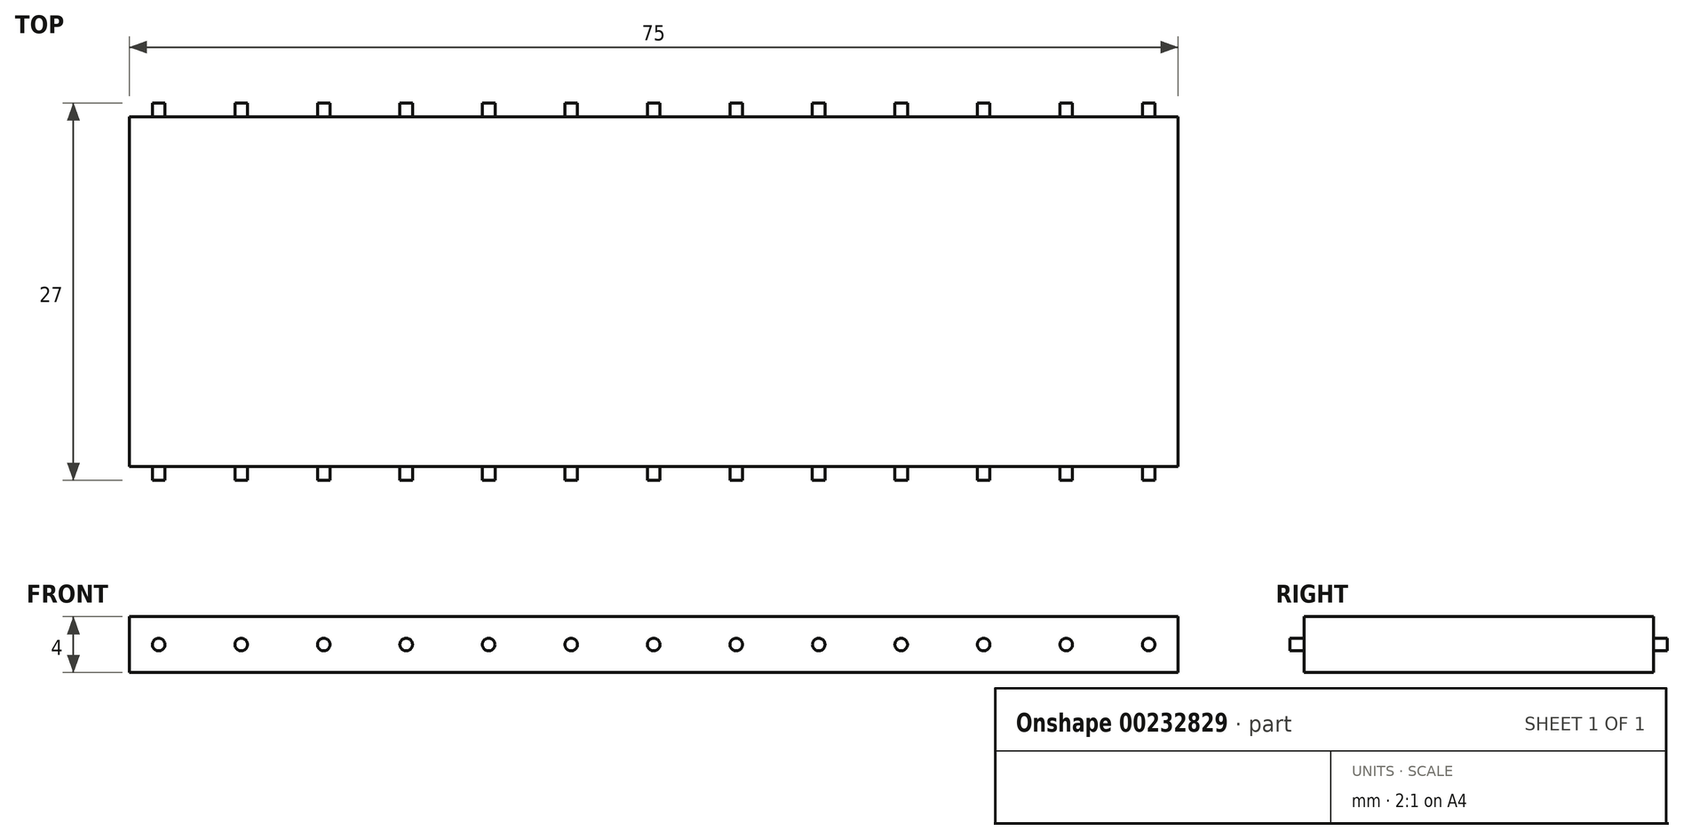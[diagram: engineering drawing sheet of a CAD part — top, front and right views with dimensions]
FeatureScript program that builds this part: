
annotation { "Feature Type Name" : "Feature", "Feature Type Description" : "" }
export const myFeature = defineFeature(function(context is Context, id is Id, definition is map)
    precondition{}
    {
        {
            var Q0;
            Q0=qCreatedBy(makeId("Top.planeOp"),FACE);
            var sketch = newSketch(context, id + "F0", { "sketchPlane" : qUnion([Q0])});
            skLineSegment(sketch, "E0.bottom", {"start": v(37.5, -12.5) * mm, "end": v(-37.5, -12.5) * mm});
            skLineSegment(sketch, "E0.top", {"start": v(37.5, 12.5) * mm, "end": v(-37.5, 12.5) * mm});
            skLineSegment(sketch, "E0.left", {"start": v(37.5, -12.5) * mm, "end": v(37.5, 12.5) * mm});
            skLineSegment(sketch, "E0.right", {"start": v(-37.5, -12.5) * mm, "end": v(-37.5, 12.5) * mm});
            skPoint(sketch, "E0.middle", {"position": v(0, 0) * mm});
            skSolve(sketch);
        }
        {
            var Q0;
            Q0=makeQuery(id+"F0.imprint","IMPRINT",FACE,{"disambiguationData":[TD([[makeQuery(id+"F0.imprint","IMPRINT",EDGE,{"derivedFrom":sQuery(id+"F0.wireOp",EDGE,"E0.bottom")}),-1.0]])]});
            extrude(context, id + "F1", {"entities" : qUnion([Q0]), "endBound" : BoundingType.SYMMETRIC, "depth" : 4 * mm});
        }
        {
            var Q0;
            Q0=qCreatedBy(makeId("Front.planeOp"),FACE);
            var sketch = newSketch(context, id + "F2", { "sketchPlane" : qUnion([Q0])});
            skCircle(sketch, "E1", {"center": v(0, 0) * mm, "radius": 0.45 * mm});
            skCircle(sketch, "E2", {"center": v(-5.9, 0) * mm, "radius": 0.45 * mm});
            skCircle(sketch, "E3", {"center": v(-11.8, 0) * mm, "radius": 0.45 * mm});
            skCircle(sketch, "E4", {"center": v(-17.7, 0) * mm, "radius": 0.45 * mm});
            skCircle(sketch, "E5", {"center": v(-23.6, 0) * mm, "radius": 0.45 * mm});
            skCircle(sketch, "E6", {"center": v(-29.5, 0) * mm, "radius": 0.45 * mm});
            skCircle(sketch, "E7", {"center": v(-35.4, 0) * mm, "radius": 0.45 * mm});
            skCircle(sketch, "E8", {"center": v(5.9, 0) * mm, "radius": 0.45 * mm});
            skCircle(sketch, "E9", {"center": v(11.8, 0) * mm, "radius": 0.45 * mm});
            skCircle(sketch, "E10", {"center": v(17.7, 0) * mm, "radius": 0.45 * mm});
            skCircle(sketch, "E11", {"center": v(23.6, 0) * mm, "radius": 0.45 * mm});
            skCircle(sketch, "E12", {"center": v(29.5, 0) * mm, "radius": 0.45 * mm});
            skCircle(sketch, "E13", {"center": v(35.4, 0) * mm, "radius": 0.45 * mm});
            skSolve(sketch);
        }
        {
            var Q0;
            Q0 = qSketchRegion(id + "F2", true);
            var Q1;
            Q1=sQuery(id+"F2.wireOp",EDGE,"E7");
            var Q2;
            Q2=sQuery(id+"F2.wireOp",EDGE,"E6");
            var Q3;
            Q3=sQuery(id+"F2.wireOp",EDGE,"E5");
            var Q4;
            Q4=sQuery(id+"F2.wireOp",EDGE,"E4");
            var Q5;
            Q5=sQuery(id+"F2.wireOp",EDGE,"E3");
            var Q6;
            Q6=sQuery(id+"F2.wireOp",EDGE,"E2");
            var Q7;
            Q7=sQuery(id+"F2.wireOp",EDGE,"E1");
            var Q8;
            Q8=sQuery(id+"F2.wireOp",EDGE,"E8");
            var Q9;
            Q9=sQuery(id+"F2.wireOp",EDGE,"E9");
            var Q10;
            Q10=sQuery(id+"F2.wireOp",EDGE,"E10");
            var Q11;
            Q11=sQuery(id+"F2.wireOp",EDGE,"E11");
            var Q12;
            Q12=sQuery(id+"F2.wireOp",EDGE,"E12");
            var Q13;
            Q13=sQuery(id+"F2.wireOp",EDGE,"E13");
            extrude(context, id + "F3", {"entities" : qUnion([Q0]), "operationType" : NewBodyOperationType.ADD, "surfaceEntities" : qUnion([Q1, Q2, Q3, Q4, Q5, Q6, Q7, Q8, Q9, Q10, Q11, Q12, Q13]), "endBound" : BoundingType.SYMMETRIC, "depth" : 27 * mm});
        }
    });
